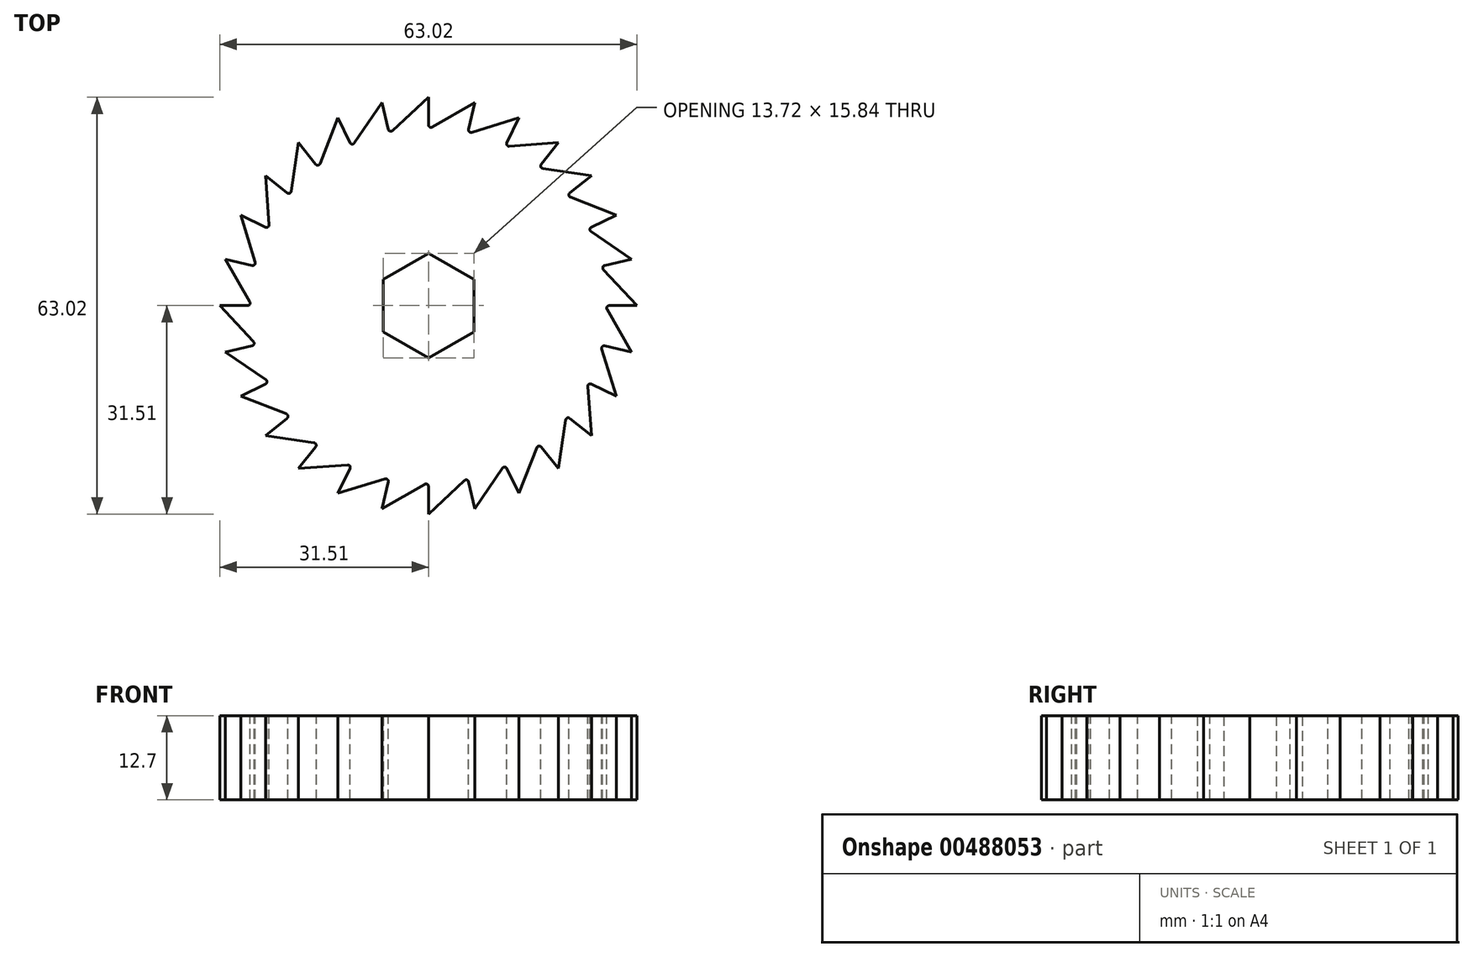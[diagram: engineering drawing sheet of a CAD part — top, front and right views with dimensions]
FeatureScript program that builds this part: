
annotation { "Feature Type Name" : "Feature", "Feature Type Description" : "" }
export const myFeature = defineFeature(function(context is Context, id is Id, definition is map)
    precondition{}
    {
        {
            var Q0;
            Q0=qCreatedBy(makeId("Top.planeOp"),FACE);
            var sketch = newSketch(context, id + "F0", { "sketchPlane" : qUnion([Q0])});
            skCircle(sketch, "E0", {"center": v(0, 0) * mm, "radius": 31.75 * mm});
            skLineSegment(sketch, "E1", {"start": v(0, 37.05) * mm, "end": v(0, -37.47) * mm, "construction": true});
            skLineSegment(sketch, "E2", {"start": v(0, 31.75) * mm, "end": v(0, 26.67) * mm});
            skLineSegment(sketch, "E3", {"start": v(0, 26.67) * mm, "end": v(7.32, 30.9) * mm});
            skLineSegment(sketch, "E4", {"start": v(0, 26.67) * mm, "end": v(0, 31.75) * mm});
            skCircle(sketch, "E5.cCircle", {"center": v(0, 0) * mm, "radius": 6.86 * mm, "construction": true});
            skLineSegment(sketch, "E5.0", {"start": v(6.86, 3.96) * mm, "end": v(6.86, -3.96) * mm});
            skLineSegment(sketch, "E5.1", {"start": v(6.86, -3.96) * mm, "end": v(0, -7.92) * mm});
            skLineSegment(sketch, "E5.2", {"start": v(0, -7.92) * mm, "end": v(-6.86, -3.96) * mm});
            skLineSegment(sketch, "E5.3", {"start": v(-6.86, -3.96) * mm, "end": v(-6.86, 3.96) * mm});
            skLineSegment(sketch, "E5.4", {"start": v(-6.86, 3.96) * mm, "end": v(0, 7.92) * mm});
            skLineSegment(sketch, "E5.5", {"start": v(0, 7.92) * mm, "end": v(6.86, 3.96) * mm});
            skPoint(sketch, "E5.0.midPoint", {"position": v(6.86, 0) * mm});
            skSolve(sketch);
        }
        {
            var Q0;
            {var subQ0=sQuery(id+"F0.wireOp",EDGE,"E3");Q0=makeQuery(id+"F0.imprint","IMPRINT",FACE,{"disambiguationData":[TD([[makeQuery(id+"F0.imprint","IMPRINT",EDGE,{"derivedFrom":subQ0}),-1.0]])]});}
            var Q1;
            {var subQ0=sQuery(id+"F0.wireOp",EDGE,"E3");Q1=makeQuery(id+"F0.imprint","IMPRINT",FACE,{"disambiguationData":[TD([[makeQuery(id+"F0.imprint","IMPRINT",EDGE,{"derivedFrom":subQ0}),1.0]])]});}
            extrude(context, id + "F1", {"entities" : qUnion([Q0, Q1]), "depth" : 12.7 * mm});
        }
        {
            var Q0;
            {var subQ0=sQuery(id+"F0.wireOp",EDGE,"E3");Q0=makeQuery(id+"F0.imprint","IMPRINT",FACE,{"disambiguationData":[TD([[makeQuery(id+"F0.imprint","IMPRINT",EDGE,{"derivedFrom":subQ0}),1.0]])]});}
            extrude(context, id + "F2", {"entities" : qUnion([Q0]), "depth" : 25 * mm});
        }
        {
            var Q0;
            Q0=makeQuery(id+"F2.opExtrude","SWEPT_BODY",BODY,{"disambiguationData":[OSD([sQuery(id+"F0.wireOp",EDGE,"E0"),sQuery(id+"F0.wireOp",EDGE,"E3"),sQuery(id+"F0.wireOp",EDGE,"E4")])]});
            var Q1;
            Q1=makeQuery(id+"F1.opExtrude","SWEPT_FACE",FACE,{"disambiguationData":[OSD([sQuery(id+"F0.wireOp",EDGE,"E0")])]});
            circularPattern(context, id + "F3", {"entities" : qUnion([Q0]), "axis" : qUnion([Q1]), "angle" : 360 * degree, "instanceCount" : 28, "equalSpace" : true});
        }
        {
            var Q0;
            Q0=makeQuery(id+"F2.opExtrude","SWEPT_BODY",BODY,{"disambiguationData":[OSD([sQuery(id+"F0.wireOp",EDGE,"E0"),sQuery(id+"F0.wireOp",EDGE,"E3"),sQuery(id+"F0.wireOp",EDGE,"E4")])]});
            var Q1;
            Q1=makeQuery(id+"F3.opPattern","COPY",BODY,{"derivedFrom":makeQuery(id+"F2.opExtrude","SWEPT_BODY",BODY,{"disambiguationData":[OSD([sQuery(id+"F0.wireOp",EDGE,"E0"),sQuery(id+"F0.wireOp",EDGE,"E3"),sQuery(id+"F0.wireOp",EDGE,"E4")])]}),"instanceName":"1"});
            var Q2;
            Q2=makeQuery(id+"F3.opPattern","COPY",BODY,{"derivedFrom":makeQuery(id+"F2.opExtrude","SWEPT_BODY",BODY,{"disambiguationData":[OSD([sQuery(id+"F0.wireOp",EDGE,"E0"),sQuery(id+"F0.wireOp",EDGE,"E3"),sQuery(id+"F0.wireOp",EDGE,"E4")])]}),"instanceName":"2"});
            var Q3;
            Q3=makeQuery(id+"F3.opPattern","COPY",BODY,{"derivedFrom":makeQuery(id+"F2.opExtrude","SWEPT_BODY",BODY,{"disambiguationData":[OSD([sQuery(id+"F0.wireOp",EDGE,"E0"),sQuery(id+"F0.wireOp",EDGE,"E3"),sQuery(id+"F0.wireOp",EDGE,"E4")])]}),"instanceName":"3"});
            var Q4;
            Q4=makeQuery(id+"F3.opPattern","COPY",BODY,{"derivedFrom":makeQuery(id+"F2.opExtrude","SWEPT_BODY",BODY,{"disambiguationData":[OSD([sQuery(id+"F0.wireOp",EDGE,"E0"),sQuery(id+"F0.wireOp",EDGE,"E3"),sQuery(id+"F0.wireOp",EDGE,"E4")])]}),"instanceName":"4"});
            var Q5;
            Q5=makeQuery(id+"F3.opPattern","COPY",BODY,{"derivedFrom":makeQuery(id+"F2.opExtrude","SWEPT_BODY",BODY,{"disambiguationData":[OSD([sQuery(id+"F0.wireOp",EDGE,"E0"),sQuery(id+"F0.wireOp",EDGE,"E3"),sQuery(id+"F0.wireOp",EDGE,"E4")])]}),"instanceName":"5"});
            var Q6;
            Q6=makeQuery(id+"F3.opPattern","COPY",BODY,{"derivedFrom":makeQuery(id+"F2.opExtrude","SWEPT_BODY",BODY,{"disambiguationData":[OSD([sQuery(id+"F0.wireOp",EDGE,"E0"),sQuery(id+"F0.wireOp",EDGE,"E3"),sQuery(id+"F0.wireOp",EDGE,"E4")])]}),"instanceName":"6"});
            var Q7;
            Q7=makeQuery(id+"F3.opPattern","COPY",BODY,{"derivedFrom":makeQuery(id+"F2.opExtrude","SWEPT_BODY",BODY,{"disambiguationData":[OSD([sQuery(id+"F0.wireOp",EDGE,"E0"),sQuery(id+"F0.wireOp",EDGE,"E3"),sQuery(id+"F0.wireOp",EDGE,"E4")])]}),"instanceName":"7"});
            var Q8;
            Q8=makeQuery(id+"F3.opPattern","COPY",BODY,{"derivedFrom":makeQuery(id+"F2.opExtrude","SWEPT_BODY",BODY,{"disambiguationData":[OSD([sQuery(id+"F0.wireOp",EDGE,"E0"),sQuery(id+"F0.wireOp",EDGE,"E3"),sQuery(id+"F0.wireOp",EDGE,"E4")])]}),"instanceName":"8"});
            var Q9;
            Q9=makeQuery(id+"F3.opPattern","COPY",BODY,{"derivedFrom":makeQuery(id+"F2.opExtrude","SWEPT_BODY",BODY,{"disambiguationData":[OSD([sQuery(id+"F0.wireOp",EDGE,"E0"),sQuery(id+"F0.wireOp",EDGE,"E3"),sQuery(id+"F0.wireOp",EDGE,"E4")])]}),"instanceName":"9"});
            var Q10;
            Q10=makeQuery(id+"F3.opPattern","COPY",BODY,{"derivedFrom":makeQuery(id+"F2.opExtrude","SWEPT_BODY",BODY,{"disambiguationData":[OSD([sQuery(id+"F0.wireOp",EDGE,"E0"),sQuery(id+"F0.wireOp",EDGE,"E3"),sQuery(id+"F0.wireOp",EDGE,"E4")])]}),"instanceName":"10"});
            var Q11;
            Q11=makeQuery(id+"F3.opPattern","COPY",BODY,{"derivedFrom":makeQuery(id+"F2.opExtrude","SWEPT_BODY",BODY,{"disambiguationData":[OSD([sQuery(id+"F0.wireOp",EDGE,"E0"),sQuery(id+"F0.wireOp",EDGE,"E3"),sQuery(id+"F0.wireOp",EDGE,"E4")])]}),"instanceName":"11"});
            var Q12;
            Q12=makeQuery(id+"F3.opPattern","COPY",BODY,{"derivedFrom":makeQuery(id+"F2.opExtrude","SWEPT_BODY",BODY,{"disambiguationData":[OSD([sQuery(id+"F0.wireOp",EDGE,"E0"),sQuery(id+"F0.wireOp",EDGE,"E3"),sQuery(id+"F0.wireOp",EDGE,"E4")])]}),"instanceName":"12"});
            var Q13;
            Q13=makeQuery(id+"F3.opPattern","COPY",BODY,{"derivedFrom":makeQuery(id+"F2.opExtrude","SWEPT_BODY",BODY,{"disambiguationData":[OSD([sQuery(id+"F0.wireOp",EDGE,"E0"),sQuery(id+"F0.wireOp",EDGE,"E3"),sQuery(id+"F0.wireOp",EDGE,"E4")])]}),"instanceName":"13"});
            var Q14;
            Q14=makeQuery(id+"F3.opPattern","COPY",BODY,{"derivedFrom":makeQuery(id+"F2.opExtrude","SWEPT_BODY",BODY,{"disambiguationData":[OSD([sQuery(id+"F0.wireOp",EDGE,"E0"),sQuery(id+"F0.wireOp",EDGE,"E3"),sQuery(id+"F0.wireOp",EDGE,"E4")])]}),"instanceName":"14"});
            var Q15;
            Q15=makeQuery(id+"F3.opPattern","COPY",BODY,{"derivedFrom":makeQuery(id+"F2.opExtrude","SWEPT_BODY",BODY,{"disambiguationData":[OSD([sQuery(id+"F0.wireOp",EDGE,"E0"),sQuery(id+"F0.wireOp",EDGE,"E3"),sQuery(id+"F0.wireOp",EDGE,"E4")])]}),"instanceName":"15"});
            var Q16;
            Q16=makeQuery(id+"F3.opPattern","COPY",BODY,{"derivedFrom":makeQuery(id+"F2.opExtrude","SWEPT_BODY",BODY,{"disambiguationData":[OSD([sQuery(id+"F0.wireOp",EDGE,"E0"),sQuery(id+"F0.wireOp",EDGE,"E3"),sQuery(id+"F0.wireOp",EDGE,"E4")])]}),"instanceName":"16"});
            var Q17;
            Q17=makeQuery(id+"F3.opPattern","COPY",BODY,{"derivedFrom":makeQuery(id+"F2.opExtrude","SWEPT_BODY",BODY,{"disambiguationData":[OSD([sQuery(id+"F0.wireOp",EDGE,"E0"),sQuery(id+"F0.wireOp",EDGE,"E3"),sQuery(id+"F0.wireOp",EDGE,"E4")])]}),"instanceName":"17"});
            var Q18;
            Q18=makeQuery(id+"F3.opPattern","COPY",BODY,{"derivedFrom":makeQuery(id+"F2.opExtrude","SWEPT_BODY",BODY,{"disambiguationData":[OSD([sQuery(id+"F0.wireOp",EDGE,"E0"),sQuery(id+"F0.wireOp",EDGE,"E3"),sQuery(id+"F0.wireOp",EDGE,"E4")])]}),"instanceName":"18"});
            var Q19;
            Q19=makeQuery(id+"F3.opPattern","COPY",BODY,{"derivedFrom":makeQuery(id+"F2.opExtrude","SWEPT_BODY",BODY,{"disambiguationData":[OSD([sQuery(id+"F0.wireOp",EDGE,"E0"),sQuery(id+"F0.wireOp",EDGE,"E3"),sQuery(id+"F0.wireOp",EDGE,"E4")])]}),"instanceName":"19"});
            var Q20;
            Q20=makeQuery(id+"F3.opPattern","COPY",BODY,{"derivedFrom":makeQuery(id+"F2.opExtrude","SWEPT_BODY",BODY,{"disambiguationData":[OSD([sQuery(id+"F0.wireOp",EDGE,"E0"),sQuery(id+"F0.wireOp",EDGE,"E3"),sQuery(id+"F0.wireOp",EDGE,"E4")])]}),"instanceName":"20"});
            var Q21;
            Q21=makeQuery(id+"F3.opPattern","COPY",BODY,{"derivedFrom":makeQuery(id+"F2.opExtrude","SWEPT_BODY",BODY,{"disambiguationData":[OSD([sQuery(id+"F0.wireOp",EDGE,"E0"),sQuery(id+"F0.wireOp",EDGE,"E3"),sQuery(id+"F0.wireOp",EDGE,"E4")])]}),"instanceName":"21"});
            var Q22;
            Q22=makeQuery(id+"F3.opPattern","COPY",BODY,{"derivedFrom":makeQuery(id+"F2.opExtrude","SWEPT_BODY",BODY,{"disambiguationData":[OSD([sQuery(id+"F0.wireOp",EDGE,"E0"),sQuery(id+"F0.wireOp",EDGE,"E3"),sQuery(id+"F0.wireOp",EDGE,"E4")])]}),"instanceName":"23"});
            var Q23;
            Q23=makeQuery(id+"F3.opPattern","COPY",BODY,{"derivedFrom":makeQuery(id+"F2.opExtrude","SWEPT_BODY",BODY,{"disambiguationData":[OSD([sQuery(id+"F0.wireOp",EDGE,"E0"),sQuery(id+"F0.wireOp",EDGE,"E3"),sQuery(id+"F0.wireOp",EDGE,"E4")])]}),"instanceName":"22"});
            var Q24;
            Q24=makeQuery(id+"F3.opPattern","COPY",BODY,{"derivedFrom":makeQuery(id+"F2.opExtrude","SWEPT_BODY",BODY,{"disambiguationData":[OSD([sQuery(id+"F0.wireOp",EDGE,"E0"),sQuery(id+"F0.wireOp",EDGE,"E3"),sQuery(id+"F0.wireOp",EDGE,"E4")])]}),"instanceName":"24"});
            var Q25;
            Q25=makeQuery(id+"F3.opPattern","COPY",BODY,{"derivedFrom":makeQuery(id+"F2.opExtrude","SWEPT_BODY",BODY,{"disambiguationData":[OSD([sQuery(id+"F0.wireOp",EDGE,"E0"),sQuery(id+"F0.wireOp",EDGE,"E3"),sQuery(id+"F0.wireOp",EDGE,"E4")])]}),"instanceName":"25"});
            var Q26;
            Q26=makeQuery(id+"F3.opPattern","COPY",BODY,{"derivedFrom":makeQuery(id+"F2.opExtrude","SWEPT_BODY",BODY,{"disambiguationData":[OSD([sQuery(id+"F0.wireOp",EDGE,"E0"),sQuery(id+"F0.wireOp",EDGE,"E3"),sQuery(id+"F0.wireOp",EDGE,"E4")])]}),"instanceName":"26"});
            var Q27;
            Q27=makeQuery(id+"F3.opPattern","COPY",BODY,{"derivedFrom":makeQuery(id+"F2.opExtrude","SWEPT_BODY",BODY,{"disambiguationData":[OSD([sQuery(id+"F0.wireOp",EDGE,"E0"),sQuery(id+"F0.wireOp",EDGE,"E3"),sQuery(id+"F0.wireOp",EDGE,"E4")])]}),"instanceName":"27"});
            var Q28;
            Q28=makeQuery(id+"F1.opExtrude","SWEPT_BODY",BODY,{"disambiguationData":[OSD([sQuery(id+"F0.wireOp",EDGE,"E0")])]});
            booleanBodies(context, id + "F4", {"operationType" : BooleanOperationType.SUBTRACTION, "tools" : qUnion([Q0, Q1, Q2, Q3, Q4, Q5, Q6, Q7, Q8, Q9, Q10, Q11, Q12, Q13, Q14, Q15, Q16, Q17, Q18, Q19, Q20, Q21, Q22, Q23, Q24, Q25, Q26, Q27]), "targets" : qUnion([Q28])});
        }
        {
            var Q0;
            Q0=makeQuery(id+"F4.opBoolean","INTERSECT",EDGE,{"derivedFrom":[makeQuery(id+"F3.opPattern","COPY",FACE,{"derivedFrom":makeQuery(id+"F2.opExtrude","SWEPT_FACE",FACE,{"disambiguationData":[OSD([sQuery(id+"F0.wireOp",EDGE,"E3")])]}),"instanceName":"20"}),makeQuery(id+"F3.opPattern","COPY",FACE,{"derivedFrom":makeQuery(id+"F2.opExtrude","SWEPT_FACE",FACE,{"disambiguationData":[OSD([sQuery(id+"F0.wireOp",EDGE,"E4")])]}),"instanceName":"21"})]});
            var Q1;
            Q1=makeQuery(id+"F4.opBoolean","INTERSECT",EDGE,{"derivedFrom":[makeQuery(id+"F3.opPattern","COPY",FACE,{"derivedFrom":makeQuery(id+"F2.opExtrude","SWEPT_FACE",FACE,{"disambiguationData":[OSD([sQuery(id+"F0.wireOp",EDGE,"E3")])]}),"instanceName":"21"}),makeQuery(id+"F3.opPattern","COPY",FACE,{"derivedFrom":makeQuery(id+"F2.opExtrude","SWEPT_FACE",FACE,{"disambiguationData":[OSD([sQuery(id+"F0.wireOp",EDGE,"E4")])]}),"instanceName":"22"})]});
            var Q2;
            Q2=makeQuery(id+"F4.opBoolean","INTERSECT",EDGE,{"derivedFrom":[makeQuery(id+"F3.opPattern","COPY",FACE,{"derivedFrom":makeQuery(id+"F2.opExtrude","SWEPT_FACE",FACE,{"disambiguationData":[OSD([sQuery(id+"F0.wireOp",EDGE,"E3")])]}),"instanceName":"22"}),makeQuery(id+"F3.opPattern","COPY",FACE,{"derivedFrom":makeQuery(id+"F2.opExtrude","SWEPT_FACE",FACE,{"disambiguationData":[OSD([sQuery(id+"F0.wireOp",EDGE,"E4")])]}),"instanceName":"23"})]});
            var Q3;
            Q3=makeQuery(id+"F4.opBoolean","INTERSECT",EDGE,{"derivedFrom":[makeQuery(id+"F3.opPattern","COPY",FACE,{"derivedFrom":makeQuery(id+"F2.opExtrude","SWEPT_FACE",FACE,{"disambiguationData":[OSD([sQuery(id+"F0.wireOp",EDGE,"E3")])]}),"instanceName":"23"}),makeQuery(id+"F3.opPattern","COPY",FACE,{"derivedFrom":makeQuery(id+"F2.opExtrude","SWEPT_FACE",FACE,{"disambiguationData":[OSD([sQuery(id+"F0.wireOp",EDGE,"E4")])]}),"instanceName":"24"})]});
            var Q4;
            Q4=makeQuery(id+"F4.opBoolean","INTERSECT",EDGE,{"derivedFrom":[makeQuery(id+"F3.opPattern","COPY",FACE,{"derivedFrom":makeQuery(id+"F2.opExtrude","SWEPT_FACE",FACE,{"disambiguationData":[OSD([sQuery(id+"F0.wireOp",EDGE,"E3")])]}),"instanceName":"24"}),makeQuery(id+"F3.opPattern","COPY",FACE,{"derivedFrom":makeQuery(id+"F2.opExtrude","SWEPT_FACE",FACE,{"disambiguationData":[OSD([sQuery(id+"F0.wireOp",EDGE,"E4")])]}),"instanceName":"25"})]});
            var Q5;
            Q5=makeQuery(id+"F4.opBoolean","INTERSECT",EDGE,{"derivedFrom":[makeQuery(id+"F3.opPattern","COPY",FACE,{"derivedFrom":makeQuery(id+"F2.opExtrude","SWEPT_FACE",FACE,{"disambiguationData":[OSD([sQuery(id+"F0.wireOp",EDGE,"E3")])]}),"instanceName":"25"}),makeQuery(id+"F3.opPattern","COPY",FACE,{"derivedFrom":makeQuery(id+"F2.opExtrude","SWEPT_FACE",FACE,{"disambiguationData":[OSD([sQuery(id+"F0.wireOp",EDGE,"E4")])]}),"instanceName":"26"})]});
            var Q6;
            Q6=makeQuery(id+"F4.opBoolean","INTERSECT",EDGE,{"derivedFrom":[makeQuery(id+"F3.opPattern","COPY",FACE,{"derivedFrom":makeQuery(id+"F2.opExtrude","SWEPT_FACE",FACE,{"disambiguationData":[OSD([sQuery(id+"F0.wireOp",EDGE,"E3")])]}),"instanceName":"26"}),makeQuery(id+"F3.opPattern","COPY",FACE,{"derivedFrom":makeQuery(id+"F2.opExtrude","SWEPT_FACE",FACE,{"disambiguationData":[OSD([sQuery(id+"F0.wireOp",EDGE,"E4")])]}),"instanceName":"27"})]});
            var Q7;
            Q7=makeQuery(id+"F4.opBoolean","INTERSECT",EDGE,{"derivedFrom":[makeQuery(id+"F2.opExtrude","SWEPT_FACE",FACE,{"disambiguationData":[OSD([sQuery(id+"F0.wireOp",EDGE,"E4")])]}),makeQuery(id+"F3.opPattern","COPY",FACE,{"derivedFrom":makeQuery(id+"F2.opExtrude","SWEPT_FACE",FACE,{"disambiguationData":[OSD([sQuery(id+"F0.wireOp",EDGE,"E3")])]}),"instanceName":"27"})]});
            var Q8;
            Q8=makeQuery(id+"F4.opBoolean","INTERSECT",EDGE,{"derivedFrom":[makeQuery(id+"F2.opExtrude","SWEPT_FACE",FACE,{"disambiguationData":[OSD([sQuery(id+"F0.wireOp",EDGE,"E3")])]}),makeQuery(id+"F3.opPattern","COPY",FACE,{"derivedFrom":makeQuery(id+"F2.opExtrude","SWEPT_FACE",FACE,{"disambiguationData":[OSD([sQuery(id+"F0.wireOp",EDGE,"E4")])]}),"instanceName":"1"})]});
            var Q9;
            Q9=makeQuery(id+"F4.opBoolean","INTERSECT",EDGE,{"derivedFrom":[makeQuery(id+"F3.opPattern","COPY",FACE,{"derivedFrom":makeQuery(id+"F2.opExtrude","SWEPT_FACE",FACE,{"disambiguationData":[OSD([sQuery(id+"F0.wireOp",EDGE,"E3")])]}),"instanceName":"1"}),makeQuery(id+"F3.opPattern","COPY",FACE,{"derivedFrom":makeQuery(id+"F2.opExtrude","SWEPT_FACE",FACE,{"disambiguationData":[OSD([sQuery(id+"F0.wireOp",EDGE,"E4")])]}),"instanceName":"2"})]});
            var Q10;
            Q10=makeQuery(id+"F4.opBoolean","INTERSECT",EDGE,{"derivedFrom":[makeQuery(id+"F3.opPattern","COPY",FACE,{"derivedFrom":makeQuery(id+"F2.opExtrude","SWEPT_FACE",FACE,{"disambiguationData":[OSD([sQuery(id+"F0.wireOp",EDGE,"E3")])]}),"instanceName":"2"}),makeQuery(id+"F3.opPattern","COPY",FACE,{"derivedFrom":makeQuery(id+"F2.opExtrude","SWEPT_FACE",FACE,{"disambiguationData":[OSD([sQuery(id+"F0.wireOp",EDGE,"E4")])]}),"instanceName":"3"})]});
            var Q11;
            Q11=makeQuery(id+"F4.opBoolean","INTERSECT",EDGE,{"derivedFrom":[makeQuery(id+"F3.opPattern","COPY",FACE,{"derivedFrom":makeQuery(id+"F2.opExtrude","SWEPT_FACE",FACE,{"disambiguationData":[OSD([sQuery(id+"F0.wireOp",EDGE,"E3")])]}),"instanceName":"3"}),makeQuery(id+"F3.opPattern","COPY",FACE,{"derivedFrom":makeQuery(id+"F2.opExtrude","SWEPT_FACE",FACE,{"disambiguationData":[OSD([sQuery(id+"F0.wireOp",EDGE,"E4")])]}),"instanceName":"4"})]});
            var Q12;
            Q12=makeQuery(id+"F4.opBoolean","INTERSECT",EDGE,{"derivedFrom":[makeQuery(id+"F3.opPattern","COPY",FACE,{"derivedFrom":makeQuery(id+"F2.opExtrude","SWEPT_FACE",FACE,{"disambiguationData":[OSD([sQuery(id+"F0.wireOp",EDGE,"E3")])]}),"instanceName":"4"}),makeQuery(id+"F3.opPattern","COPY",FACE,{"derivedFrom":makeQuery(id+"F2.opExtrude","SWEPT_FACE",FACE,{"disambiguationData":[OSD([sQuery(id+"F0.wireOp",EDGE,"E4")])]}),"instanceName":"5"})]});
            var Q13;
            Q13=makeQuery(id+"F4.opBoolean","INTERSECT",EDGE,{"derivedFrom":[makeQuery(id+"F3.opPattern","COPY",FACE,{"derivedFrom":makeQuery(id+"F2.opExtrude","SWEPT_FACE",FACE,{"disambiguationData":[OSD([sQuery(id+"F0.wireOp",EDGE,"E3")])]}),"instanceName":"5"}),makeQuery(id+"F3.opPattern","COPY",FACE,{"derivedFrom":makeQuery(id+"F2.opExtrude","SWEPT_FACE",FACE,{"disambiguationData":[OSD([sQuery(id+"F0.wireOp",EDGE,"E4")])]}),"instanceName":"6"})]});
            var Q14;
            Q14=makeQuery(id+"F4.opBoolean","INTERSECT",EDGE,{"derivedFrom":[makeQuery(id+"F3.opPattern","COPY",FACE,{"derivedFrom":makeQuery(id+"F2.opExtrude","SWEPT_FACE",FACE,{"disambiguationData":[OSD([sQuery(id+"F0.wireOp",EDGE,"E3")])]}),"instanceName":"6"}),makeQuery(id+"F3.opPattern","COPY",FACE,{"derivedFrom":makeQuery(id+"F2.opExtrude","SWEPT_FACE",FACE,{"disambiguationData":[OSD([sQuery(id+"F0.wireOp",EDGE,"E4")])]}),"instanceName":"7"})]});
            var Q15;
            Q15=makeQuery(id+"F4.opBoolean","INTERSECT",EDGE,{"derivedFrom":[makeQuery(id+"F3.opPattern","COPY",FACE,{"derivedFrom":makeQuery(id+"F2.opExtrude","SWEPT_FACE",FACE,{"disambiguationData":[OSD([sQuery(id+"F0.wireOp",EDGE,"E3")])]}),"instanceName":"7"}),makeQuery(id+"F3.opPattern","COPY",FACE,{"derivedFrom":makeQuery(id+"F2.opExtrude","SWEPT_FACE",FACE,{"disambiguationData":[OSD([sQuery(id+"F0.wireOp",EDGE,"E4")])]}),"instanceName":"8"})]});
            var Q16;
            Q16=makeQuery(id+"F4.opBoolean","INTERSECT",EDGE,{"derivedFrom":[makeQuery(id+"F3.opPattern","COPY",FACE,{"derivedFrom":makeQuery(id+"F2.opExtrude","SWEPT_FACE",FACE,{"disambiguationData":[OSD([sQuery(id+"F0.wireOp",EDGE,"E3")])]}),"instanceName":"8"}),makeQuery(id+"F3.opPattern","COPY",FACE,{"derivedFrom":makeQuery(id+"F2.opExtrude","SWEPT_FACE",FACE,{"disambiguationData":[OSD([sQuery(id+"F0.wireOp",EDGE,"E4")])]}),"instanceName":"9"})]});
            var Q17;
            Q17=makeQuery(id+"F4.opBoolean","INTERSECT",EDGE,{"derivedFrom":[makeQuery(id+"F3.opPattern","COPY",FACE,{"derivedFrom":makeQuery(id+"F2.opExtrude","SWEPT_FACE",FACE,{"disambiguationData":[OSD([sQuery(id+"F0.wireOp",EDGE,"E3")])]}),"instanceName":"9"}),makeQuery(id+"F3.opPattern","COPY",FACE,{"derivedFrom":makeQuery(id+"F2.opExtrude","SWEPT_FACE",FACE,{"disambiguationData":[OSD([sQuery(id+"F0.wireOp",EDGE,"E4")])]}),"instanceName":"10"})]});
            var Q18;
            Q18=makeQuery(id+"F4.opBoolean","INTERSECT",EDGE,{"derivedFrom":[makeQuery(id+"F3.opPattern","COPY",FACE,{"derivedFrom":makeQuery(id+"F2.opExtrude","SWEPT_FACE",FACE,{"disambiguationData":[OSD([sQuery(id+"F0.wireOp",EDGE,"E3")])]}),"instanceName":"10"}),makeQuery(id+"F3.opPattern","COPY",FACE,{"derivedFrom":makeQuery(id+"F2.opExtrude","SWEPT_FACE",FACE,{"disambiguationData":[OSD([sQuery(id+"F0.wireOp",EDGE,"E4")])]}),"instanceName":"11"})]});
            var Q19;
            Q19=makeQuery(id+"F4.opBoolean","INTERSECT",EDGE,{"derivedFrom":[makeQuery(id+"F3.opPattern","COPY",FACE,{"derivedFrom":makeQuery(id+"F2.opExtrude","SWEPT_FACE",FACE,{"disambiguationData":[OSD([sQuery(id+"F0.wireOp",EDGE,"E3")])]}),"instanceName":"11"}),makeQuery(id+"F3.opPattern","COPY",FACE,{"derivedFrom":makeQuery(id+"F2.opExtrude","SWEPT_FACE",FACE,{"disambiguationData":[OSD([sQuery(id+"F0.wireOp",EDGE,"E4")])]}),"instanceName":"12"})]});
            var Q20;
            Q20=makeQuery(id+"F4.opBoolean","INTERSECT",EDGE,{"derivedFrom":[makeQuery(id+"F3.opPattern","COPY",FACE,{"derivedFrom":makeQuery(id+"F2.opExtrude","SWEPT_FACE",FACE,{"disambiguationData":[OSD([sQuery(id+"F0.wireOp",EDGE,"E3")])]}),"instanceName":"12"}),makeQuery(id+"F3.opPattern","COPY",FACE,{"derivedFrom":makeQuery(id+"F2.opExtrude","SWEPT_FACE",FACE,{"disambiguationData":[OSD([sQuery(id+"F0.wireOp",EDGE,"E4")])]}),"instanceName":"13"})]});
            var Q21;
            Q21=makeQuery(id+"F4.opBoolean","INTERSECT",EDGE,{"derivedFrom":[makeQuery(id+"F3.opPattern","COPY",FACE,{"derivedFrom":makeQuery(id+"F2.opExtrude","SWEPT_FACE",FACE,{"disambiguationData":[OSD([sQuery(id+"F0.wireOp",EDGE,"E3")])]}),"instanceName":"13"}),makeQuery(id+"F3.opPattern","COPY",FACE,{"derivedFrom":makeQuery(id+"F2.opExtrude","SWEPT_FACE",FACE,{"disambiguationData":[OSD([sQuery(id+"F0.wireOp",EDGE,"E4")])]}),"instanceName":"14"})]});
            var Q22;
            Q22=makeQuery(id+"F4.opBoolean","INTERSECT",EDGE,{"derivedFrom":[makeQuery(id+"F3.opPattern","COPY",FACE,{"derivedFrom":makeQuery(id+"F2.opExtrude","SWEPT_FACE",FACE,{"disambiguationData":[OSD([sQuery(id+"F0.wireOp",EDGE,"E3")])]}),"instanceName":"14"}),makeQuery(id+"F3.opPattern","COPY",FACE,{"derivedFrom":makeQuery(id+"F2.opExtrude","SWEPT_FACE",FACE,{"disambiguationData":[OSD([sQuery(id+"F0.wireOp",EDGE,"E4")])]}),"instanceName":"15"})]});
            var Q23;
            Q23=makeQuery(id+"F4.opBoolean","INTERSECT",EDGE,{"derivedFrom":[makeQuery(id+"F3.opPattern","COPY",FACE,{"derivedFrom":makeQuery(id+"F2.opExtrude","SWEPT_FACE",FACE,{"disambiguationData":[OSD([sQuery(id+"F0.wireOp",EDGE,"E3")])]}),"instanceName":"15"}),makeQuery(id+"F3.opPattern","COPY",FACE,{"derivedFrom":makeQuery(id+"F2.opExtrude","SWEPT_FACE",FACE,{"disambiguationData":[OSD([sQuery(id+"F0.wireOp",EDGE,"E4")])]}),"instanceName":"16"})]});
            var Q24;
            Q24=makeQuery(id+"F4.opBoolean","INTERSECT",EDGE,{"derivedFrom":[makeQuery(id+"F3.opPattern","COPY",FACE,{"derivedFrom":makeQuery(id+"F2.opExtrude","SWEPT_FACE",FACE,{"disambiguationData":[OSD([sQuery(id+"F0.wireOp",EDGE,"E3")])]}),"instanceName":"16"}),makeQuery(id+"F3.opPattern","COPY",FACE,{"derivedFrom":makeQuery(id+"F2.opExtrude","SWEPT_FACE",FACE,{"disambiguationData":[OSD([sQuery(id+"F0.wireOp",EDGE,"E4")])]}),"instanceName":"17"})]});
            var Q25;
            Q25=makeQuery(id+"F4.opBoolean","INTERSECT",EDGE,{"derivedFrom":[makeQuery(id+"F3.opPattern","COPY",FACE,{"derivedFrom":makeQuery(id+"F2.opExtrude","SWEPT_FACE",FACE,{"disambiguationData":[OSD([sQuery(id+"F0.wireOp",EDGE,"E3")])]}),"instanceName":"17"}),makeQuery(id+"F3.opPattern","COPY",FACE,{"derivedFrom":makeQuery(id+"F2.opExtrude","SWEPT_FACE",FACE,{"disambiguationData":[OSD([sQuery(id+"F0.wireOp",EDGE,"E4")])]}),"instanceName":"18"})]});
            var Q26;
            Q26=makeQuery(id+"F4.opBoolean","INTERSECT",EDGE,{"derivedFrom":[makeQuery(id+"F3.opPattern","COPY",FACE,{"derivedFrom":makeQuery(id+"F2.opExtrude","SWEPT_FACE",FACE,{"disambiguationData":[OSD([sQuery(id+"F0.wireOp",EDGE,"E3")])]}),"instanceName":"18"}),makeQuery(id+"F3.opPattern","COPY",FACE,{"derivedFrom":makeQuery(id+"F2.opExtrude","SWEPT_FACE",FACE,{"disambiguationData":[OSD([sQuery(id+"F0.wireOp",EDGE,"E4")])]}),"instanceName":"19"})]});
            var Q27;
            Q27=makeQuery(id+"F4.opBoolean","INTERSECT",EDGE,{"derivedFrom":[makeQuery(id+"F3.opPattern","COPY",FACE,{"derivedFrom":makeQuery(id+"F2.opExtrude","SWEPT_FACE",FACE,{"disambiguationData":[OSD([sQuery(id+"F0.wireOp",EDGE,"E3")])]}),"instanceName":"19"}),makeQuery(id+"F3.opPattern","COPY",FACE,{"derivedFrom":makeQuery(id+"F2.opExtrude","SWEPT_FACE",FACE,{"disambiguationData":[OSD([sQuery(id+"F0.wireOp",EDGE,"E4")])]}),"instanceName":"20"})]});
            var Q28;
            Q28=makeQuery(id+"F4.opBoolean","COPY",EDGE,{"derivedFrom":makeQuery(id+"F3.opPattern","COPY",EDGE,{"derivedFrom":makeQuery(id+"F2.opExtrude","SWEPT_EDGE",EDGE,{"disambiguationData":[OSD([sQuery(id+"F0.wireOp",EDGE,"E3"),sQuery(id+"F0.wireOp",EDGE,"E4")])]}),"instanceName":"6"})});
            var Q29;
            Q29=makeQuery(id+"F4.opBoolean","COPY",EDGE,{"derivedFrom":makeQuery(id+"F3.opPattern","COPY",EDGE,{"derivedFrom":makeQuery(id+"F2.opExtrude","SWEPT_EDGE",EDGE,{"disambiguationData":[OSD([sQuery(id+"F0.wireOp",EDGE,"E3"),sQuery(id+"F0.wireOp",EDGE,"E4")])]}),"instanceName":"7"})});
            var Q30;
            Q30=makeQuery(id+"F4.opBoolean","COPY",EDGE,{"derivedFrom":makeQuery(id+"F3.opPattern","COPY",EDGE,{"derivedFrom":makeQuery(id+"F2.opExtrude","SWEPT_EDGE",EDGE,{"disambiguationData":[OSD([sQuery(id+"F0.wireOp",EDGE,"E3"),sQuery(id+"F0.wireOp",EDGE,"E4")])]}),"instanceName":"8"})});
            var Q31;
            Q31=makeQuery(id+"F4.opBoolean","COPY",EDGE,{"derivedFrom":makeQuery(id+"F3.opPattern","COPY",EDGE,{"derivedFrom":makeQuery(id+"F2.opExtrude","SWEPT_EDGE",EDGE,{"disambiguationData":[OSD([sQuery(id+"F0.wireOp",EDGE,"E3"),sQuery(id+"F0.wireOp",EDGE,"E4")])]}),"instanceName":"9"})});
            var Q32;
            Q32=makeQuery(id+"F4.opBoolean","COPY",EDGE,{"derivedFrom":makeQuery(id+"F3.opPattern","COPY",EDGE,{"derivedFrom":makeQuery(id+"F2.opExtrude","SWEPT_EDGE",EDGE,{"disambiguationData":[OSD([sQuery(id+"F0.wireOp",EDGE,"E3"),sQuery(id+"F0.wireOp",EDGE,"E4")])]}),"instanceName":"10"})});
            var Q33;
            Q33=makeQuery(id+"F4.opBoolean","COPY",EDGE,{"derivedFrom":makeQuery(id+"F3.opPattern","COPY",EDGE,{"derivedFrom":makeQuery(id+"F2.opExtrude","SWEPT_EDGE",EDGE,{"disambiguationData":[OSD([sQuery(id+"F0.wireOp",EDGE,"E3"),sQuery(id+"F0.wireOp",EDGE,"E4")])]}),"instanceName":"11"})});
            var Q34;
            Q34=makeQuery(id+"F4.opBoolean","COPY",EDGE,{"derivedFrom":makeQuery(id+"F3.opPattern","COPY",EDGE,{"derivedFrom":makeQuery(id+"F2.opExtrude","SWEPT_EDGE",EDGE,{"disambiguationData":[OSD([sQuery(id+"F0.wireOp",EDGE,"E3"),sQuery(id+"F0.wireOp",EDGE,"E4")])]}),"instanceName":"12"})});
            var Q35;
            Q35=makeQuery(id+"F4.opBoolean","COPY",EDGE,{"derivedFrom":makeQuery(id+"F3.opPattern","COPY",EDGE,{"derivedFrom":makeQuery(id+"F2.opExtrude","SWEPT_EDGE",EDGE,{"disambiguationData":[OSD([sQuery(id+"F0.wireOp",EDGE,"E3"),sQuery(id+"F0.wireOp",EDGE,"E4")])]}),"instanceName":"13"})});
            var Q36;
            Q36=makeQuery(id+"F4.opBoolean","COPY",EDGE,{"derivedFrom":makeQuery(id+"F3.opPattern","COPY",EDGE,{"derivedFrom":makeQuery(id+"F2.opExtrude","SWEPT_EDGE",EDGE,{"disambiguationData":[OSD([sQuery(id+"F0.wireOp",EDGE,"E3"),sQuery(id+"F0.wireOp",EDGE,"E4")])]}),"instanceName":"14"})});
            var Q37;
            Q37=makeQuery(id+"F4.opBoolean","COPY",EDGE,{"derivedFrom":makeQuery(id+"F3.opPattern","COPY",EDGE,{"derivedFrom":makeQuery(id+"F2.opExtrude","SWEPT_EDGE",EDGE,{"disambiguationData":[OSD([sQuery(id+"F0.wireOp",EDGE,"E3"),sQuery(id+"F0.wireOp",EDGE,"E4")])]}),"instanceName":"15"})});
            var Q38;
            Q38=makeQuery(id+"F4.opBoolean","COPY",EDGE,{"derivedFrom":makeQuery(id+"F3.opPattern","COPY",EDGE,{"derivedFrom":makeQuery(id+"F2.opExtrude","SWEPT_EDGE",EDGE,{"disambiguationData":[OSD([sQuery(id+"F0.wireOp",EDGE,"E3"),sQuery(id+"F0.wireOp",EDGE,"E4")])]}),"instanceName":"16"})});
            var Q39;
            Q39=makeQuery(id+"F4.opBoolean","COPY",EDGE,{"derivedFrom":makeQuery(id+"F3.opPattern","COPY",EDGE,{"derivedFrom":makeQuery(id+"F2.opExtrude","SWEPT_EDGE",EDGE,{"disambiguationData":[OSD([sQuery(id+"F0.wireOp",EDGE,"E3"),sQuery(id+"F0.wireOp",EDGE,"E4")])]}),"instanceName":"17"})});
            var Q40;
            Q40=makeQuery(id+"F4.opBoolean","COPY",EDGE,{"derivedFrom":makeQuery(id+"F3.opPattern","COPY",EDGE,{"derivedFrom":makeQuery(id+"F2.opExtrude","SWEPT_EDGE",EDGE,{"disambiguationData":[OSD([sQuery(id+"F0.wireOp",EDGE,"E3"),sQuery(id+"F0.wireOp",EDGE,"E4")])]}),"instanceName":"18"})});
            var Q41;
            Q41=makeQuery(id+"F4.opBoolean","COPY",EDGE,{"derivedFrom":makeQuery(id+"F3.opPattern","COPY",EDGE,{"derivedFrom":makeQuery(id+"F2.opExtrude","SWEPT_EDGE",EDGE,{"disambiguationData":[OSD([sQuery(id+"F0.wireOp",EDGE,"E3"),sQuery(id+"F0.wireOp",EDGE,"E4")])]}),"instanceName":"19"})});
            var Q42;
            Q42=makeQuery(id+"F4.opBoolean","COPY",EDGE,{"derivedFrom":makeQuery(id+"F3.opPattern","COPY",EDGE,{"derivedFrom":makeQuery(id+"F2.opExtrude","SWEPT_EDGE",EDGE,{"disambiguationData":[OSD([sQuery(id+"F0.wireOp",EDGE,"E3"),sQuery(id+"F0.wireOp",EDGE,"E4")])]}),"instanceName":"20"})});
            var Q43;
            Q43=makeQuery(id+"F4.opBoolean","COPY",EDGE,{"derivedFrom":makeQuery(id+"F3.opPattern","COPY",EDGE,{"derivedFrom":makeQuery(id+"F2.opExtrude","SWEPT_EDGE",EDGE,{"disambiguationData":[OSD([sQuery(id+"F0.wireOp",EDGE,"E3"),sQuery(id+"F0.wireOp",EDGE,"E4")])]}),"instanceName":"21"})});
            var Q44;
            Q44=makeQuery(id+"F4.opBoolean","COPY",EDGE,{"derivedFrom":makeQuery(id+"F3.opPattern","COPY",EDGE,{"derivedFrom":makeQuery(id+"F2.opExtrude","SWEPT_EDGE",EDGE,{"disambiguationData":[OSD([sQuery(id+"F0.wireOp",EDGE,"E3"),sQuery(id+"F0.wireOp",EDGE,"E4")])]}),"instanceName":"22"})});
            var Q45;
            Q45=makeQuery(id+"F4.opBoolean","COPY",EDGE,{"derivedFrom":makeQuery(id+"F3.opPattern","COPY",EDGE,{"derivedFrom":makeQuery(id+"F2.opExtrude","SWEPT_EDGE",EDGE,{"disambiguationData":[OSD([sQuery(id+"F0.wireOp",EDGE,"E3"),sQuery(id+"F0.wireOp",EDGE,"E4")])]}),"instanceName":"23"})});
            var Q46;
            Q46=makeQuery(id+"F4.opBoolean","COPY",EDGE,{"derivedFrom":makeQuery(id+"F3.opPattern","COPY",EDGE,{"derivedFrom":makeQuery(id+"F2.opExtrude","SWEPT_EDGE",EDGE,{"disambiguationData":[OSD([sQuery(id+"F0.wireOp",EDGE,"E3"),sQuery(id+"F0.wireOp",EDGE,"E4")])]}),"instanceName":"24"})});
            var Q47;
            Q47=makeQuery(id+"F4.opBoolean","COPY",EDGE,{"derivedFrom":makeQuery(id+"F3.opPattern","COPY",EDGE,{"derivedFrom":makeQuery(id+"F2.opExtrude","SWEPT_EDGE",EDGE,{"disambiguationData":[OSD([sQuery(id+"F0.wireOp",EDGE,"E3"),sQuery(id+"F0.wireOp",EDGE,"E4")])]}),"instanceName":"25"})});
            var Q48;
            Q48=makeQuery(id+"F4.opBoolean","COPY",EDGE,{"derivedFrom":makeQuery(id+"F3.opPattern","COPY",EDGE,{"derivedFrom":makeQuery(id+"F2.opExtrude","SWEPT_EDGE",EDGE,{"disambiguationData":[OSD([sQuery(id+"F0.wireOp",EDGE,"E3"),sQuery(id+"F0.wireOp",EDGE,"E4")])]}),"instanceName":"26"})});
            var Q49;
            Q49=makeQuery(id+"F4.opBoolean","COPY",EDGE,{"derivedFrom":makeQuery(id+"F3.opPattern","COPY",EDGE,{"derivedFrom":makeQuery(id+"F2.opExtrude","SWEPT_EDGE",EDGE,{"disambiguationData":[OSD([sQuery(id+"F0.wireOp",EDGE,"E3"),sQuery(id+"F0.wireOp",EDGE,"E4")])]}),"instanceName":"27"})});
            var Q50;
            Q50=makeQuery(id+"F4.opBoolean","COPY",EDGE,{"derivedFrom":makeQuery(id+"F2.opExtrude","SWEPT_EDGE",EDGE,{"disambiguationData":[OSD([sQuery(id+"F0.wireOp",EDGE,"E3"),sQuery(id+"F0.wireOp",EDGE,"E4")])]})});
            var Q51;
            Q51=makeQuery(id+"F4.opBoolean","COPY",EDGE,{"derivedFrom":makeQuery(id+"F3.opPattern","COPY",EDGE,{"derivedFrom":makeQuery(id+"F2.opExtrude","SWEPT_EDGE",EDGE,{"disambiguationData":[OSD([sQuery(id+"F0.wireOp",EDGE,"E3"),sQuery(id+"F0.wireOp",EDGE,"E4")])]}),"instanceName":"1"})});
            var Q52;
            Q52=makeQuery(id+"F4.opBoolean","COPY",EDGE,{"derivedFrom":makeQuery(id+"F3.opPattern","COPY",EDGE,{"derivedFrom":makeQuery(id+"F2.opExtrude","SWEPT_EDGE",EDGE,{"disambiguationData":[OSD([sQuery(id+"F0.wireOp",EDGE,"E3"),sQuery(id+"F0.wireOp",EDGE,"E4")])]}),"instanceName":"2"})});
            var Q53;
            Q53=makeQuery(id+"F4.opBoolean","COPY",EDGE,{"derivedFrom":makeQuery(id+"F3.opPattern","COPY",EDGE,{"derivedFrom":makeQuery(id+"F2.opExtrude","SWEPT_EDGE",EDGE,{"disambiguationData":[OSD([sQuery(id+"F0.wireOp",EDGE,"E3"),sQuery(id+"F0.wireOp",EDGE,"E4")])]}),"instanceName":"3"})});
            var Q54;
            Q54=makeQuery(id+"F4.opBoolean","COPY",EDGE,{"derivedFrom":makeQuery(id+"F3.opPattern","COPY",EDGE,{"derivedFrom":makeQuery(id+"F2.opExtrude","SWEPT_EDGE",EDGE,{"disambiguationData":[OSD([sQuery(id+"F0.wireOp",EDGE,"E3"),sQuery(id+"F0.wireOp",EDGE,"E4")])]}),"instanceName":"4"})});
            var Q55;
            Q55=makeQuery(id+"F4.opBoolean","COPY",EDGE,{"derivedFrom":makeQuery(id+"F3.opPattern","COPY",EDGE,{"derivedFrom":makeQuery(id+"F2.opExtrude","SWEPT_EDGE",EDGE,{"disambiguationData":[OSD([sQuery(id+"F0.wireOp",EDGE,"E3"),sQuery(id+"F0.wireOp",EDGE,"E4")])]}),"instanceName":"5"})});
            fillet(context, id + "F5", {"entities" : qUnion([Q0, Q1, Q2, Q3, Q4, Q5, Q6, Q7, Q8, Q9, Q10, Q11, Q12, Q13, Q14, Q15, Q16, Q17, Q18, Q19, Q20, Q21, Q22, Q23, Q24, Q25, Q26, Q27, Q28, Q29, Q30, Q31, Q32, Q33, Q34, Q35, Q36, Q37, Q38, Q39, Q40, Q41, Q42, Q43, Q44, Q45, Q46, Q47, Q48, Q49, Q50, Q51, Q52, Q53, Q54, Q55]), "radius" : 0.38 * mm, "tangentPropagation" : true, "allowEdgeOverflow" : false});
        }
    });
